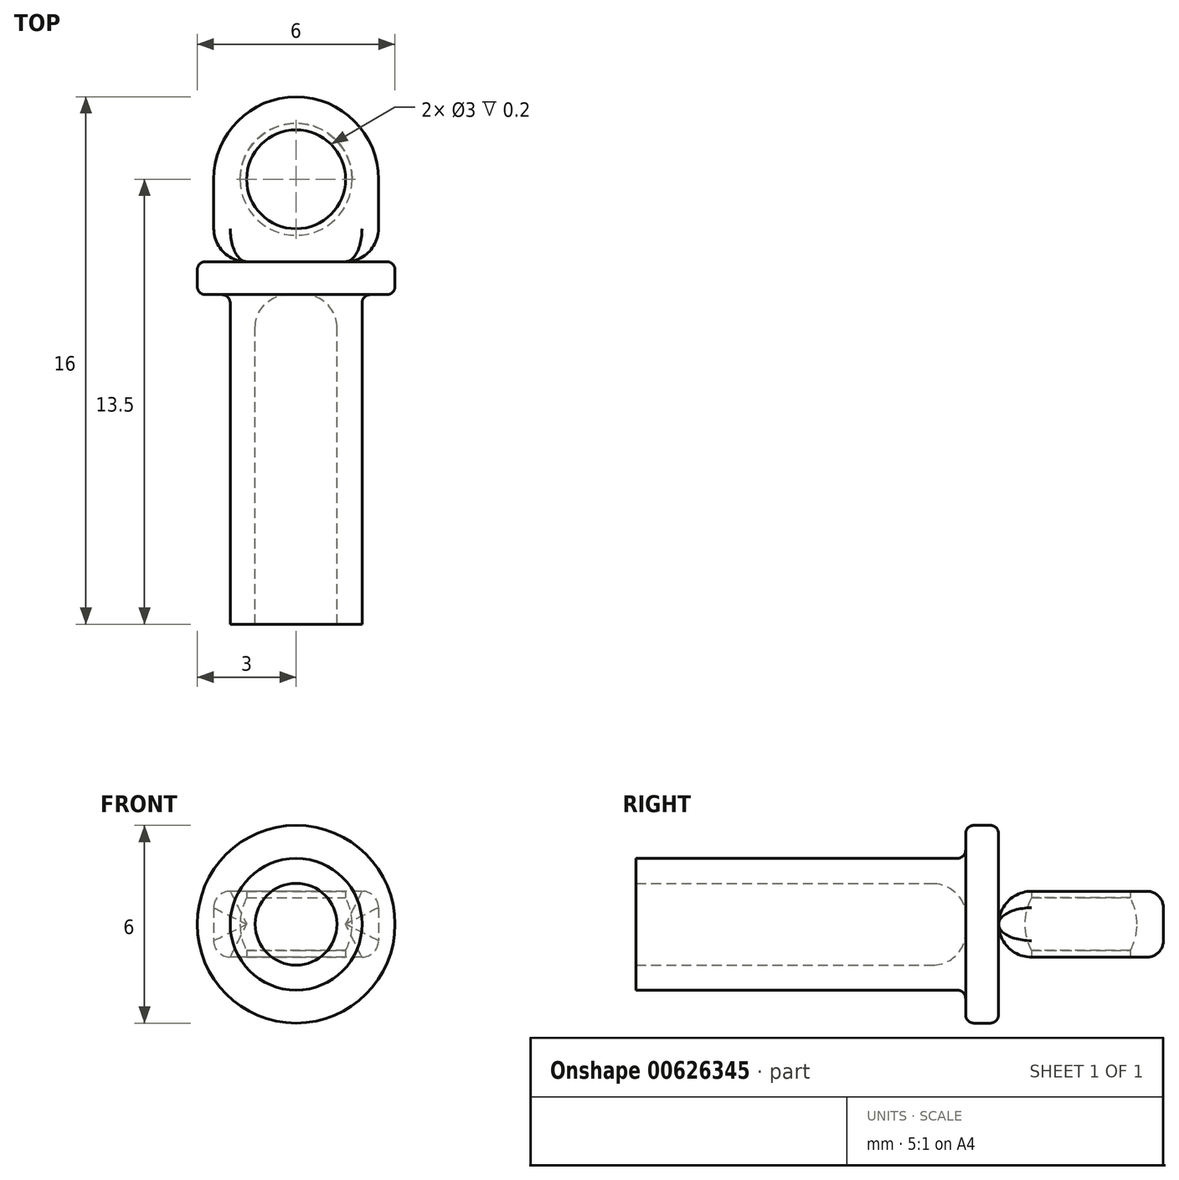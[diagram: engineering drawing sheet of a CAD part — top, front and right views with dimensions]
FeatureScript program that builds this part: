
annotation { "Feature Type Name" : "Feature", "Feature Type Description" : "" }
export const myFeature = defineFeature(function(context is Context, id is Id, definition is map)
    precondition{}
    {
        {
            var Q0;
            Q0=qCreatedBy(makeId("Top.planeOp"),FACE);
            var sketch = newSketch(context, id + "F0", { "sketchPlane" : qUnion([Q0])});
            skLineSegment(sketch, "E0", {"start": v(3, 0) * mm, "end": v(0, 0) * mm});
            skLineSegment(sketch, "E1.MirrorCS", {"start": v(2, -1) * mm, "end": v(3, -1) * mm});
            skLineSegment(sketch, "E2.MirrorCS", {"start": v(0, 0) * mm, "end": v(0, -1) * mm});
            skLineSegment(sketch, "E3.MirrorCS", {"start": v(0, -1) * mm, "end": v(0.24, -1) * mm});
            skLineSegment(sketch, "E4.MirrorCS", {"start": v(1.24, -11) * mm, "end": v(1.24, -2) * mm});
            skLineSegment(sketch, "E5.MirrorCS", {"start": v(3, -1) * mm, "end": v(3, 0) * mm});
            skLineSegment(sketch, "E6.MirrorCS", {"start": v(1.24, -11) * mm, "end": v(2, -11) * mm});
            skLineSegment(sketch, "E7.MirrorCS", {"start": v(2, -11) * mm, "end": v(2, -1) * mm});
            skLineSegment(sketch, "E8.bottom", {"start": v(2.5, 0) * mm, "end": v(-2.5, 0) * mm});
            skLineSegment(sketch, "E8.left", {"start": v(2.5, 0) * mm, "end": v(2.5, 2.5) * mm});
            skLineSegment(sketch, "E8.right", {"start": v(-2.5, 0) * mm, "end": v(-2.5, 2.5) * mm});
            skCircle(sketch, "E9", {"center": v(0, 2.5) * mm, "radius": 1.5 * mm});
            skLineSegment(sketch, "E10", {"start": v(0, 0) * mm, "end": v(0, 13.43) * mm, "construction": true});
            skLineSegment(sketch, "E11", {"start": v(-2.5, 2.5) * mm, "end": v(2.5, 2.5) * mm, "construction": true});
            skArc(sketch, "E12", {"start": v(2.5, 2.5) * mm, "mid": v(0, 5) * mm, "end": v(-2.5, 2.5) * mm});
            skPoint(sketch, "E12.third.point", {"position": v(0, 5) * mm});
            skPoint(sketch, "E13.visualSharp", {"position": v(1.24, -1) * mm});
            skArc(sketch, "E13.filletArc", {"start": v(1.24, -2) * mm, "mid": v(0.95, -1.3) * mm, "end": v(0.24, -1) * mm});
            skSolve(sketch);
        }
        {
            var Q0;
            {var subQ1=sQuery(id+"F0.wireOp",EDGE,"E0");Q0=makeQuery(id+"F0.imprint","IMPRINT",FACE,{"disambiguationData":[TD([[makeQuery(id+"F0.imprint","IMPRINT",EDGE,{"derivedFrom":subQ1}),1.0]])]});}
            var Q1;
            Q1=sQuery(id+"F0.wireOp",EDGE,"E5.MirrorCS");
            var Q2;
            Q2=sQuery(id+"F0.wireOp",EDGE,"E0");
            var Q3;
            Q3=sQuery(id+"F0.wireOp",EDGE,"E1.MirrorCS");
            var Q4;
            Q4=sQuery(id+"F0.wireOp",EDGE,"E7.MirrorCS");
            var Q5;
            Q5=sQuery(id+"F0.wireOp",EDGE,"E6.MirrorCS");
            var Q6;
            Q6=sQuery(id+"F0.wireOp",EDGE,"E4.MirrorCS");
            var Q7;
            Q7=sQuery(id+"F0.wireOp",EDGE,"E3.MirrorCS");
            var Q8;
            Q8=sQuery(id+"F0.wireOp",EDGE,"E2.MirrorCS");
            revolve(context, id + "F1", {"surfaceOperationType" : NewSurfaceOperationType.NEW, "entities" : qUnion([Q0]), "surfaceEntities" : qUnion([Q1, Q2, Q3, Q4, Q5, Q6, Q7]), "axis" : qUnion([Q8]), "revolveType" : RevolveType.FULL});
        }
        {
            var Q0;
            {var subQ1=sQuery(id+"F0.wireOp",EDGE,"E8.left");Q0=makeQuery(id+"F0.imprint","IMPRINT",FACE,{"disambiguationData":[TD([[makeQuery(id+"F0.imprint","IMPRINT",EDGE,{"derivedFrom":subQ1}),1.0]])]});}
            var Q1;
            Q1=sQuery(id+"F0.wireOp",EDGE,"E8.bottom");
            var Q2;
            Q2=sQuery(id+"F0.wireOp",EDGE,"E8.right");
            var Q3;
            Q3=sQuery(id+"F0.wireOp",EDGE,"E12");
            var Q4;
            Q4=sQuery(id+"F0.wireOp",EDGE,"E8.left");
            var Q5;
            Q5=sQuery(id+"F0.wireOp",EDGE,"E9");
            extrude(context, id + "F2", {"entities" : qUnion([Q0]), "surfaceEntities" : qUnion([Q1, Q2, Q3, Q4, Q5]), "endBound" : BoundingType.SYMMETRIC, "depth" : 2 * mm, "offsetDistance" : 25 * mm});
        }
        {
            var Q0;
            Q0=makeQuery(id+"F0.imprint","IMPRINT",FACE,{"disambiguationData":[TD([[makeQuery(id+"F0.imprint","IMPRINT",EDGE,{"derivedFrom":sQuery(id+"F0.wireOp",EDGE,"E9")}),1.0]])]});
            var sketch = newSketch(context, id + "F3", { "sketchPlane" : qUnion([Q0])});
            skArc(sketch, "E14", {"start": v(1.7, 2.5) * mm, "mid": v(0, 4.2) * mm, "end": v(-1.7, 2.5) * mm});
            skLineSegment(sketch, "E15", {"start": v(-1.7, 2.5) * mm, "end": v(1.7, 2.5) * mm});
            skSolve(sketch);
        }
        {
            var Q0;
            Q0 = qSketchRegion(id + "F3", true);
            var Q1;
            Q1 = qConstructionFilter(qBodyType(qCreatedBy(id + "F3" ,EDGE), BodyType.WIRE), ConstructionObject.NO);
            var Q2;
            Q2=sQuery(id+"F3.wireOp",EDGE,"E15");
            revolve(context, id + "F4", {"operationType" : NewBodyOperationType.REMOVE, "surfaceOperationType" : NewSurfaceOperationType.NEW, "entities" : qUnion([Q0]), "surfaceEntities" : qUnion([Q1]), "axis" : qUnion([Q2]), "revolveType" : RevolveType.FULL, "oppositeDirection" : true});
        }
        {
            var Q0;
            Q0=makeQuery(id+"F2.opExtrude","CAP_EDGE",EDGE,{"disambiguationData":[OSD([sQuery(id+"F0.wireOp",EDGE,"E12")])],"isStart":false});
            var Q1;
            Q1=makeQuery(id+"F2.opExtrude","CAP_EDGE",EDGE,{"disambiguationData":[OSD([sQuery(id+"F0.wireOp",EDGE,"E12")])],"isStart":true});
            fillet(context, id + "F5", {"entities" : qUnion([Q0, Q1]), "radius" : 0.5 * mm, "tangentPropagation" : true, "allowEdgeOverflow" : false});
        }
        {
            var Q0;
            Q0=makeQuery(id+"F1.opRevolve","SWEPT_EDGE",EDGE,{"disambiguationData":[OSD([sQuery(id+"F0.wireOp",EDGE,"E0"),sQuery(id+"F0.wireOp",EDGE,"E5.MirrorCS")])]});
            var Q1;
            Q1=makeQuery(id+"F1.opRevolve","SWEPT_EDGE",EDGE,{"disambiguationData":[OSD([sQuery(id+"F0.wireOp",EDGE,"E1.MirrorCS"),sQuery(id+"F0.wireOp",EDGE,"E5.MirrorCS")])]});
            fillet(context, id + "F6", {"entities" : qUnion([Q0, Q1]), "radius" : 0.25 * mm, "tangentPropagation" : true, "allowEdgeOverflow" : false});
        }
        {
            var Q0;
            Q0=makeQuery(id+"F2.opExtrude","CAP_EDGE",EDGE,{"disambiguationData":[OSD([sQuery(id+"F0.wireOp",EDGE,"E8.bottom")])],"isStart":true});
            fillet(context, id + "F7", {"entities" : qUnion([Q0]), "radius" : 1 * mm, "tangentPropagation" : true, "allowEdgeOverflow" : false});
        }
        {
            var Q0;
            Q0=makeQuery(id+"F1.opRevolve","SWEPT_EDGE",EDGE,{"disambiguationData":[OSD([sQuery(id+"F0.wireOp",EDGE,"E1.MirrorCS"),sQuery(id+"F0.wireOp",EDGE,"E7.MirrorCS")])]});
            fillet(context, id + "F8", {"entities" : qUnion([Q0]), "radius" : .25 * mm, "tangentPropagation" : true, "allowEdgeOverflow" : false});
        }
    });
